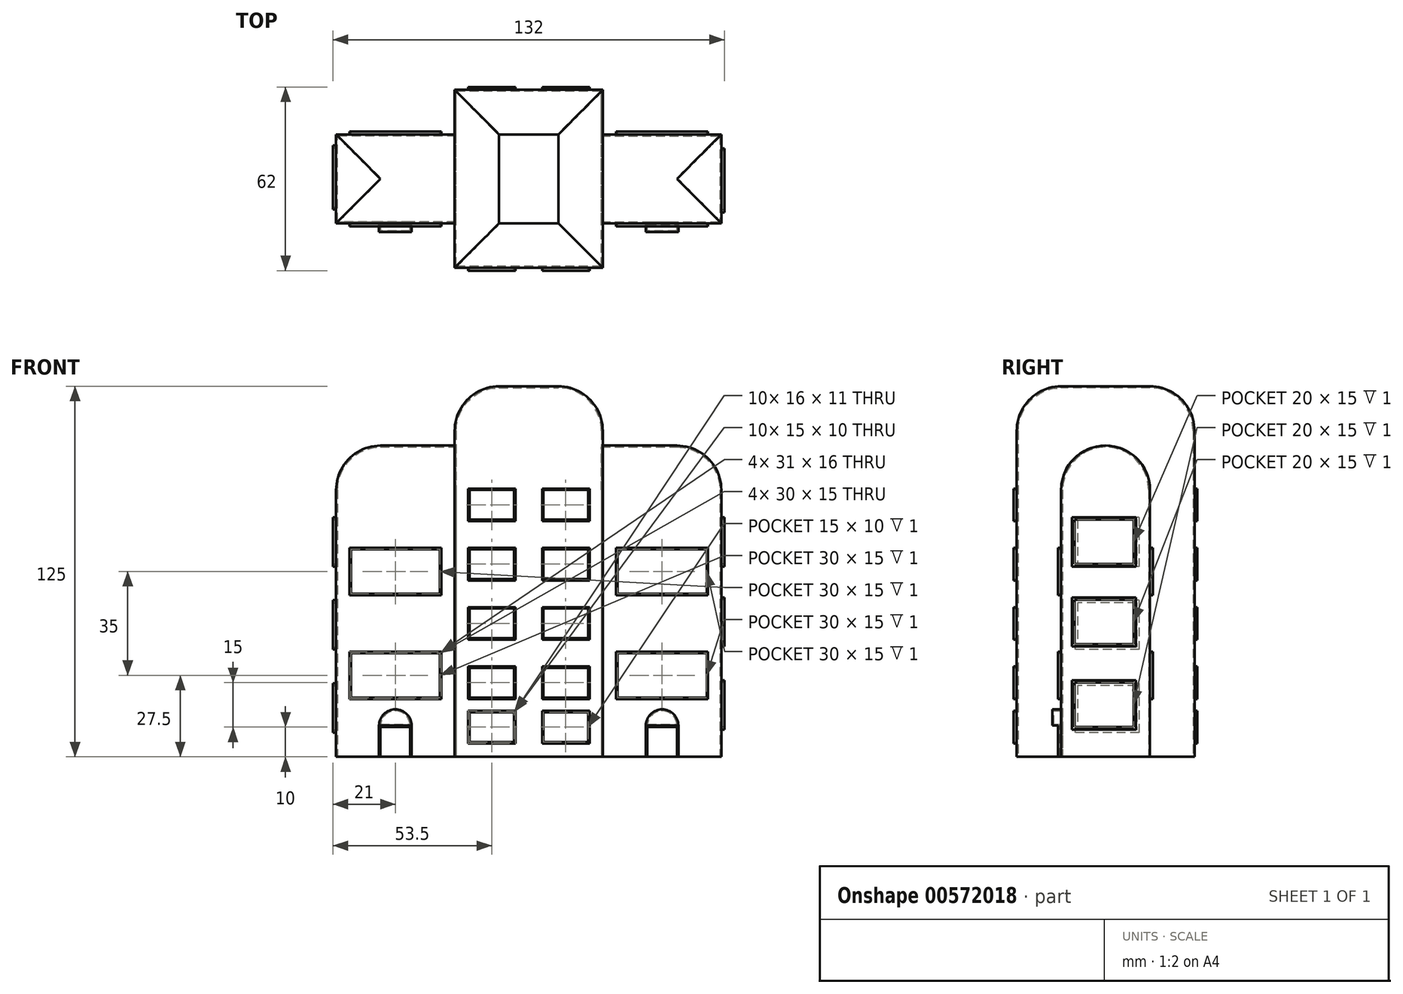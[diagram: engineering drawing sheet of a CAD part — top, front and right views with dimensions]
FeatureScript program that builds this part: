
annotation { "Feature Type Name" : "Feature", "Feature Type Description" : "" }
export const myFeature = defineFeature(function(context is Context, id is Id, definition is map)
    precondition{}
    {
        {
            var Q0;
            Q0=qCreatedBy(makeId("Top.planeOp"),FACE);
            var sketch = newSketch(context, id + "F0", { "sketchPlane" : qUnion([Q0])});
            skLineSegment(sketch, "E0.bottom", {"start": v(25, -30) * mm, "end": v(-25, -30) * mm});
            skLineSegment(sketch, "E0.top", {"start": v(25, 30) * mm, "end": v(-25, 30) * mm});
            skLineSegment(sketch, "E0.left", {"start": v(25, -30) * mm, "end": v(25, 30) * mm});
            skLineSegment(sketch, "E0.right", {"start": v(-25, -30) * mm, "end": v(-25, 30) * mm});
            skPoint(sketch, "E0.middle", {"position": v(0, 0) * mm});
            skLineSegment(sketch, "E1", {"start": v(0, 0) * mm, "end": v(90, 0) * mm, "construction": true});
            skPoint(sketch, "E1.endSnap0", {"position": v(25, 0) * mm});
            skLineSegment(sketch, "E2", {"start": v(0, 0) * mm, "end": v(-90, 0) * mm, "construction": true});
            skLineSegment(sketch, "E3.bottom", {"start": v(25, 15) * mm, "end": v(65, 15) * mm});
            skLineSegment(sketch, "E3.top", {"start": v(25, -15) * mm, "end": v(65, -15) * mm});
            skLineSegment(sketch, "E3.left", {"start": v(25, 15) * mm, "end": v(25, -15) * mm});
            skLineSegment(sketch, "E3.right", {"start": v(65, 15) * mm, "end": v(65, -15) * mm});
            skPoint(sketch, "E3.middle", {"position": v(45, 0) * mm});
            skLineSegment(sketch, "E4.bottom", {"start": v(-25, -15) * mm, "end": v(-65, -15) * mm});
            skLineSegment(sketch, "E4.top", {"start": v(-25, 15) * mm, "end": v(-65, 15) * mm});
            skLineSegment(sketch, "E4.left", {"start": v(-25, -15) * mm, "end": v(-25, 15) * mm});
            skLineSegment(sketch, "E4.right", {"start": v(-65, -15) * mm, "end": v(-65, 15) * mm});
            skPoint(sketch, "E4.middle", {"position": v(-45, 0) * mm});
            skSolve(sketch);
        }
        {
            var Q0;
            {var subQ3=sQuery(id+"F0.wireOp",EDGE,"E0.bottom");Q0=makeQuery(id+"F0.imprint","IMPRINT",FACE,{"disambiguationData":[TD([[makeQuery(id+"F0.imprint","IMPRINT",EDGE,{"derivedFrom":subQ3}),-1.0]])]});}
            extrude(context, id + "F1", {"entities" : qUnion([Q0]), "depth" : 100 * mm, "offsetDistance" : 25 * mm});
        }
        {
            var Q0;
            Q0=makeQuery(id+"F0.imprint","IMPRINT",FACE,{"disambiguationData":[TD([[makeQuery(id+"F0.imprint","IMPRINT",EDGE,{"derivedFrom":sQuery(id+"F0.wireOp",EDGE,"E4.bottom")}),-1.0]])]});
            var Q1;
            Q1=makeQuery(id+"F0.imprint","IMPRINT",FACE,{"disambiguationData":[TD([[makeQuery(id+"F0.imprint","IMPRINT",EDGE,{"derivedFrom":sQuery(id+"F0.wireOp",EDGE,"E3.bottom")}),-1.0]])]});
            extrude(context, id + "F2", {"entities" : qUnion([Q0, Q1]), "operationType" : NewBodyOperationType.ADD, "depth" : 80 * mm, "offsetDistance" : 25 * mm});
        }
        {
            var Q0;
            Q0=makeQuery(id+"F1.opExtrude","SWEPT_FACE",FACE,{"disambiguationData":[OSD([sQuery(id+"F0.wireOp",EDGE,"E0.bottom")])]});
            var sketch = newSketch(context, id + "F3", { "sketchPlane" : qUnion([Q0])});
            skLineSegment(sketch, "E5.bottom", {"start": v(-20, 90) * mm, "end": v(-5, 90) * mm});
            skLineSegment(sketch, "E5.top", {"start": v(-20, 80) * mm, "end": v(-5, 80) * mm});
            skLineSegment(sketch, "E5.left", {"start": v(-20, 90) * mm, "end": v(-20, 80) * mm});
            skLineSegment(sketch, "E5.right", {"start": v(-5, 90) * mm, "end": v(-5, 80) * mm});
            skLineSegment(sketch, "E6.bottom", {"start": v(5, 90) * mm, "end": v(20, 90) * mm});
            skLineSegment(sketch, "E6.top", {"start": v(5, 80) * mm, "end": v(20, 80) * mm});
            skLineSegment(sketch, "E6.left", {"start": v(5, 90) * mm, "end": v(5, 80) * mm});
            skLineSegment(sketch, "E6.right", {"start": v(20, 90) * mm, "end": v(20, 80) * mm});
            skLineSegment(sketch, "E7.0", {"start": v(-20.5, 90.5) * mm, "end": v(-4.5, 90.5) * mm});
            skLineSegment(sketch, "E7.1", {"start": v(-20.5, 90.5) * mm, "end": v(-20.5, 79.5) * mm});
            skLineSegment(sketch, "E7.2", {"start": v(-20.5, 79.5) * mm, "end": v(-4.5, 79.5) * mm});
            skLineSegment(sketch, "E7.3", {"start": v(-4.5, 90.5) * mm, "end": v(-4.5, 79.5) * mm});
            skLineSegment(sketch, "E8.0", {"start": v(4.5, 90.5) * mm, "end": v(20.5, 90.5) * mm});
            skLineSegment(sketch, "E8.1", {"start": v(4.5, 90.5) * mm, "end": v(4.5, 79.5) * mm});
            skLineSegment(sketch, "E8.2", {"start": v(4.5, 79.5) * mm, "end": v(20.5, 79.5) * mm});
            skLineSegment(sketch, "E8.3", {"start": v(20.5, 90.5) * mm, "end": v(20.5, 79.5) * mm});
            skLineSegment(sketch, "E9.bottom", {"start": v(-20, 70) * mm, "end": v(-5, 70) * mm});
            skLineSegment(sketch, "E9.top", {"start": v(-20, 60) * mm, "end": v(-5, 60) * mm});
            skLineSegment(sketch, "E9.left", {"start": v(-20, 70) * mm, "end": v(-20, 60) * mm});
            skLineSegment(sketch, "E9.right", {"start": v(-5, 70) * mm, "end": v(-5, 60) * mm});
            skLineSegment(sketch, "E10.bottom", {"start": v(5, 70) * mm, "end": v(20, 70) * mm});
            skLineSegment(sketch, "E10.top", {"start": v(5, 60) * mm, "end": v(20, 60) * mm});
            skLineSegment(sketch, "E10.left", {"start": v(5, 70) * mm, "end": v(5, 60) * mm});
            skLineSegment(sketch, "E10.right", {"start": v(20, 70) * mm, "end": v(20, 60) * mm});
            skLineSegment(sketch, "E11.0", {"start": v(-20.5, 70.5) * mm, "end": v(-4.5, 70.5) * mm});
            skLineSegment(sketch, "E11.1", {"start": v(-20.5, 70.5) * mm, "end": v(-20.5, 59.5) * mm});
            skLineSegment(sketch, "E11.2", {"start": v(-20.5, 59.5) * mm, "end": v(-4.5, 59.5) * mm});
            skLineSegment(sketch, "E11.3", {"start": v(-4.5, 70.5) * mm, "end": v(-4.5, 59.5) * mm});
            skLineSegment(sketch, "E12.0", {"start": v(4.5, 70.5) * mm, "end": v(4.5, 59.5) * mm});
            skLineSegment(sketch, "E12.1", {"start": v(4.5, 70.5) * mm, "end": v(20.5, 70.5) * mm});
            skLineSegment(sketch, "E12.2", {"start": v(20.5, 70.5) * mm, "end": v(20.5, 59.5) * mm});
            skLineSegment(sketch, "E12.3", {"start": v(4.5, 59.5) * mm, "end": v(20.5, 59.5) * mm});
            skLineSegment(sketch, "E13.bottom", {"start": v(-20, 50) * mm, "end": v(-5, 50) * mm});
            skLineSegment(sketch, "E13.top", {"start": v(-20, 40) * mm, "end": v(-5, 40) * mm});
            skLineSegment(sketch, "E13.left", {"start": v(-20, 50) * mm, "end": v(-20, 40) * mm});
            skLineSegment(sketch, "E13.right", {"start": v(-5, 50) * mm, "end": v(-5, 40) * mm});
            skLineSegment(sketch, "E14.bottom", {"start": v(5, 50) * mm, "end": v(20, 50) * mm});
            skLineSegment(sketch, "E14.top", {"start": v(5, 40) * mm, "end": v(20, 40) * mm});
            skLineSegment(sketch, "E14.left", {"start": v(5, 50) * mm, "end": v(5, 40) * mm});
            skLineSegment(sketch, "E14.right", {"start": v(20, 50) * mm, "end": v(20, 40) * mm});
            skLineSegment(sketch, "E15.bottom", {"start": v(-20, 30) * mm, "end": v(-5, 30) * mm});
            skLineSegment(sketch, "E15.top", {"start": v(-20, 20) * mm, "end": v(-5, 20) * mm});
            skLineSegment(sketch, "E15.left", {"start": v(-20, 30) * mm, "end": v(-20, 20) * mm});
            skLineSegment(sketch, "E15.right", {"start": v(-5, 30) * mm, "end": v(-5, 20) * mm});
            skLineSegment(sketch, "E16.bottom", {"start": v(5, 30) * mm, "end": v(20, 30) * mm});
            skLineSegment(sketch, "E16.top", {"start": v(5, 20) * mm, "end": v(20, 20) * mm});
            skLineSegment(sketch, "E16.left", {"start": v(5, 30) * mm, "end": v(5, 20) * mm});
            skLineSegment(sketch, "E16.right", {"start": v(20, 30) * mm, "end": v(20, 20) * mm});
            skLineSegment(sketch, "E17.bottom", {"start": v(-20, 15) * mm, "end": v(-5, 15) * mm});
            skLineSegment(sketch, "E17.top", {"start": v(-20, 5) * mm, "end": v(-5, 5) * mm});
            skLineSegment(sketch, "E17.left", {"start": v(-20, 15) * mm, "end": v(-20, 5) * mm});
            skLineSegment(sketch, "E17.right", {"start": v(-5, 15) * mm, "end": v(-5, 5) * mm});
            skLineSegment(sketch, "E18.bottom", {"start": v(5, 15) * mm, "end": v(20, 15) * mm});
            skLineSegment(sketch, "E18.top", {"start": v(5, 5) * mm, "end": v(20, 5) * mm});
            skLineSegment(sketch, "E18.left", {"start": v(5, 15) * mm, "end": v(5, 5) * mm});
            skLineSegment(sketch, "E18.right", {"start": v(20, 15) * mm, "end": v(20, 5) * mm});
            skLineSegment(sketch, "E19.0", {"start": v(-20.5, 50.5) * mm, "end": v(-4.5, 50.5) * mm});
            skLineSegment(sketch, "E19.1", {"start": v(-20.5, 50.5) * mm, "end": v(-20.5, 39.5) * mm});
            skLineSegment(sketch, "E19.2", {"start": v(-20.5, 39.5) * mm, "end": v(-4.5, 39.5) * mm});
            skLineSegment(sketch, "E19.3", {"start": v(-4.5, 50.5) * mm, "end": v(-4.5, 39.5) * mm});
            skLineSegment(sketch, "E20.0", {"start": v(4.5, 50.5) * mm, "end": v(4.5, 39.5) * mm});
            skLineSegment(sketch, "E20.1", {"start": v(4.5, 50.5) * mm, "end": v(20.5, 50.5) * mm});
            skLineSegment(sketch, "E20.2", {"start": v(20.5, 50.5) * mm, "end": v(20.5, 39.5) * mm});
            skLineSegment(sketch, "E20.3", {"start": v(4.5, 39.5) * mm, "end": v(20.5, 39.5) * mm});
            skLineSegment(sketch, "E21.0", {"start": v(-20.5, 30.5) * mm, "end": v(-4.5, 30.5) * mm});
            skLineSegment(sketch, "E21.1", {"start": v(-20.5, 30.5) * mm, "end": v(-20.5, 19.5) * mm});
            skLineSegment(sketch, "E21.2", {"start": v(-20.5, 19.5) * mm, "end": v(-4.5, 19.5) * mm});
            skLineSegment(sketch, "E21.3", {"start": v(-4.5, 30.5) * mm, "end": v(-4.5, 19.5) * mm});
            skLineSegment(sketch, "E22.0", {"start": v(4.5, 30.5) * mm, "end": v(20.5, 30.5) * mm});
            skLineSegment(sketch, "E22.1", {"start": v(4.5, 30.5) * mm, "end": v(4.5, 19.5) * mm});
            skLineSegment(sketch, "E22.2", {"start": v(4.5, 19.5) * mm, "end": v(20.5, 19.5) * mm});
            skLineSegment(sketch, "E22.3", {"start": v(20.5, 30.5) * mm, "end": v(20.5, 19.5) * mm});
            skLineSegment(sketch, "E23.0", {"start": v(-20.5, 15.5) * mm, "end": v(-4.5, 15.5) * mm});
            skLineSegment(sketch, "E23.1", {"start": v(-20.5, 15.5) * mm, "end": v(-20.5, 4.5) * mm});
            skLineSegment(sketch, "E23.2", {"start": v(-20.5, 4.5) * mm, "end": v(-4.5, 4.5) * mm});
            skLineSegment(sketch, "E23.3", {"start": v(-4.5, 15.5) * mm, "end": v(-4.5, 4.5) * mm});
            skLineSegment(sketch, "E24.0", {"start": v(4.5, 15.5) * mm, "end": v(20.5, 15.5) * mm});
            skLineSegment(sketch, "E24.1", {"start": v(4.5, 15.5) * mm, "end": v(4.5, 4.5) * mm});
            skLineSegment(sketch, "E24.2", {"start": v(4.5, 4.5) * mm, "end": v(20.5, 4.5) * mm});
            skLineSegment(sketch, "E24.3", {"start": v(20.5, 15.5) * mm, "end": v(20.5, 4.5) * mm});
            skSolve(sketch);
        }
        {
            var Q0;
            Q0=makeQuery(id+"F3.imprint","IMPRINT",FACE,{"disambiguationData":[TD([[makeQuery(id+"F3.imprint","IMPRINT",EDGE,{"derivedFrom":sQuery(id+"F3.wireOp",EDGE,"E5.bottom")}),1.0]])]});
            var Q1;
            Q1=makeQuery(id+"F3.imprint","IMPRINT",FACE,{"disambiguationData":[TD([[makeQuery(id+"F3.imprint","IMPRINT",EDGE,{"derivedFrom":sQuery(id+"F3.wireOp",EDGE,"E6.bottom")}),1.0]])]});
            var Q2;
            Q2=makeQuery(id+"F3.imprint","IMPRINT",FACE,{"disambiguationData":[TD([[makeQuery(id+"F3.imprint","IMPRINT",EDGE,{"derivedFrom":sQuery(id+"F3.wireOp",EDGE,"E10.bottom")}),1.0]])]});
            var Q3;
            Q3=makeQuery(id+"F3.imprint","IMPRINT",FACE,{"disambiguationData":[TD([[makeQuery(id+"F3.imprint","IMPRINT",EDGE,{"derivedFrom":sQuery(id+"F3.wireOp",EDGE,"E9.bottom")}),1.0]])]});
            var Q4;
            Q4=makeQuery(id+"F3.imprint","IMPRINT",FACE,{"disambiguationData":[TD([[makeQuery(id+"F3.imprint","IMPRINT",EDGE,{"derivedFrom":sQuery(id+"F3.wireOp",EDGE,"E13.bottom")}),1.0]])]});
            var Q5;
            Q5=makeQuery(id+"F3.imprint","IMPRINT",FACE,{"disambiguationData":[TD([[makeQuery(id+"F3.imprint","IMPRINT",EDGE,{"derivedFrom":sQuery(id+"F3.wireOp",EDGE,"E14.bottom")}),1.0]])]});
            var Q6;
            Q6=makeQuery(id+"F3.imprint","IMPRINT",FACE,{"disambiguationData":[TD([[makeQuery(id+"F3.imprint","IMPRINT",EDGE,{"derivedFrom":sQuery(id+"F3.wireOp",EDGE,"E16.bottom")}),1.0]])]});
            var Q7;
            Q7=makeQuery(id+"F3.imprint","IMPRINT",FACE,{"disambiguationData":[TD([[makeQuery(id+"F3.imprint","IMPRINT",EDGE,{"derivedFrom":sQuery(id+"F3.wireOp",EDGE,"E15.bottom")}),1.0]])]});
            var Q8;
            Q8=makeQuery(id+"F3.imprint","IMPRINT",FACE,{"disambiguationData":[TD([[makeQuery(id+"F3.imprint","IMPRINT",EDGE,{"derivedFrom":sQuery(id+"F3.wireOp",EDGE,"E17.bottom")}),1.0]])]});
            var Q9;
            Q9=makeQuery(id+"F3.imprint","IMPRINT",FACE,{"disambiguationData":[TD([[makeQuery(id+"F3.imprint","IMPRINT",EDGE,{"derivedFrom":sQuery(id+"F3.wireOp",EDGE,"E18.bottom")}),1.0]])]});
            extrude(context, id + "F4", {"entities" : qUnion([Q0, Q1, Q2, Q3, Q4, Q5, Q6, Q7, Q8, Q9]), "operationType" : NewBodyOperationType.ADD, "depth" : 1 * mm, "offsetDistance" : 25 * mm, "hasSecondDirection" : true, "secondDirectionOppositeDirection" : true, "secondDirectionDepth" : 61 * mm});
        }
        {
            var Q0;
            Q0=makeQuery(id+"F2.opExtrude","SWEPT_FACE",FACE,{"disambiguationData":[OSD([sQuery(id+"F0.wireOp",EDGE,"E4.bottom")])]});
            var sketch = newSketch(context, id + "F5", { "sketchPlane" : qUnion([Q0])});
            skLineSegment(sketch, "E25", {"start": v(-50, 0) * mm, "end": v(-50, 10) * mm});
            skLineSegment(sketch, "E26", {"start": v(-50, 10) * mm, "end": v(-45, 10) * mm});
            skLineSegment(sketch, "E27", {"start": v(-45, 10) * mm, "end": v(-45, 0) * mm});
            skLineSegment(sketch, "E28", {"start": v(-45, 10) * mm, "end": v(-40, 10) * mm});
            skLineSegment(sketch, "E29", {"start": v(-40, 10) * mm, "end": v(-40, 0) * mm});
            skLineSegment(sketch, "E30", {"start": v(-50, 0) * mm, "end": v(-40, 0) * mm});
            skLineSegment(sketch, "E31.0", {"start": v(-45, 5) * mm, "end": v(-40, 5) * mm});
            skLineSegment(sketch, "E31.1", {"start": v(-50, 5) * mm, "end": v(-45, 5) * mm});
            skLineSegment(sketch, "E32.0", {"start": v(-39.5, 10.5) * mm, "end": v(-39.5, 0) * mm});
            skLineSegment(sketch, "E32.1", {"start": v(-45, 10.5) * mm, "end": v(-39.5, 10.5) * mm});
            skLineSegment(sketch, "E32.2", {"start": v(-50.5, 10.5) * mm, "end": v(-45, 10.5) * mm});
            skLineSegment(sketch, "E32.3", {"start": v(-50.5, 0) * mm, "end": v(-50.5, 10.5) * mm});
            skArc(sketch, "E33", {"start": v(-39.5, 10.5) * mm, "mid": v(-45, 16) * mm, "end": v(-50.5, 10.5) * mm});
            skLineSegment(sketch, "E34.bottom", {"start": v(-60, 35) * mm, "end": v(-30, 35) * mm});
            skLineSegment(sketch, "E34.top", {"start": v(-60, 20) * mm, "end": v(-30, 20) * mm});
            skLineSegment(sketch, "E34.left", {"start": v(-60, 35) * mm, "end": v(-60, 20) * mm});
            skLineSegment(sketch, "E34.right", {"start": v(-30, 35) * mm, "end": v(-30, 20) * mm});
            skLineSegment(sketch, "E35.0", {"start": v(-60.5, 35.5) * mm, "end": v(-29.5, 35.5) * mm});
            skLineSegment(sketch, "E35.1", {"start": v(-60.5, 35.5) * mm, "end": v(-60.5, 19.5) * mm});
            skLineSegment(sketch, "E35.2", {"start": v(-60.5, 19.5) * mm, "end": v(-29.5, 19.5) * mm});
            skLineSegment(sketch, "E35.3", {"start": v(-29.5, 35.5) * mm, "end": v(-29.5, 19.5) * mm});
            skLineSegment(sketch, "E36.bottom", {"start": v(-60, 70) * mm, "end": v(-30, 70) * mm});
            skLineSegment(sketch, "E36.top", {"start": v(-60, 55) * mm, "end": v(-30, 55) * mm});
            skLineSegment(sketch, "E36.left", {"start": v(-60, 70) * mm, "end": v(-60, 55) * mm});
            skLineSegment(sketch, "E36.right", {"start": v(-30, 70) * mm, "end": v(-30, 55) * mm});
            skLineSegment(sketch, "E37.0", {"start": v(-60.5, 70.5) * mm, "end": v(-29.5, 70.5) * mm});
            skLineSegment(sketch, "E37.1", {"start": v(-60.5, 70.5) * mm, "end": v(-60.5, 54.5) * mm});
            skLineSegment(sketch, "E37.2", {"start": v(-60.5, 54.5) * mm, "end": v(-29.5, 54.5) * mm});
            skLineSegment(sketch, "E37.3", {"start": v(-29.5, 70.5) * mm, "end": v(-29.5, 54.5) * mm});
            skSolve(sketch);
        }
        {
            var Q0;
            {var subQ11=sQuery(id+"F5.wireOp",EDGE,"E26");Q0=makeQuery(id+"F5.imprint","IMPRINT",FACE,{"disambiguationData":[TD([[makeQuery(id+"F5.imprint","IMPRINT",EDGE,{"derivedFrom":subQ11}),1.0]])]});}
            extrude(context, id + "F6", {"entities" : qUnion([Q0]), "operationType" : NewBodyOperationType.ADD, "depth" : 1 * mm, "offsetDistance" : 25 * mm});
        }
        {
            var Q0;
            Q0=makeQuery(id+"F5.imprint","IMPRINT",FACE,{"disambiguationData":[TD([[makeQuery(id+"F5.imprint","IMPRINT",EDGE,{"derivedFrom":sQuery(id+"F5.wireOp",EDGE,"E32.1")}),1.0]])]});
            extrude(context, id + "F7", {"entities" : qUnion([Q0]), "operationType" : NewBodyOperationType.ADD, "depth" : 3 * mm, "offsetDistance" : 25 * mm});
        }
        {
            var Q0;
            {var subQ0=sQuery(id+"F5.wireOp",EDGE,"E26");Q0=makeQuery(id+"F5.imprint","IMPRINT",FACE,{"disambiguationData":[TD([[makeQuery(id+"F5.imprint","IMPRINT",EDGE,{"derivedFrom":subQ0}),-1.0]])]});}
            var Q1;
            {var subQ3=sQuery(id+"F5.wireOp",EDGE,"E31.1");Q1=makeQuery(id+"F5.imprint","IMPRINT",FACE,{"disambiguationData":[TD([[makeQuery(id+"F5.imprint","IMPRINT",EDGE,{"derivedFrom":subQ3}),-1.0]])]});}
            var Q2;
            {var subQ3=sQuery(id+"F5.wireOp",EDGE,"E31.0");Q2=makeQuery(id+"F5.imprint","IMPRINT",FACE,{"disambiguationData":[TD([[makeQuery(id+"F5.imprint","IMPRINT",EDGE,{"derivedFrom":subQ3}),-1.0]])]});}
            var Q3;
            {var subQ0=sQuery(id+"F5.wireOp",EDGE,"E28");Q3=makeQuery(id+"F5.imprint","IMPRINT",FACE,{"disambiguationData":[TD([[makeQuery(id+"F5.imprint","IMPRINT",EDGE,{"derivedFrom":subQ0}),-1.0]])]});}
            extrude(context, id + "F8", {"entities" : qUnion([Q0, Q1, Q2, Q3]), "operationType" : NewBodyOperationType.ADD, "depth" : .5 * mm, "offsetDistance" : 25 * mm});
        }
        {
            var Q0;
            Q0=makeQuery(id+"F5.imprint","IMPRINT",FACE,{"disambiguationData":[TD([[makeQuery(id+"F5.imprint","IMPRINT",EDGE,{"derivedFrom":sQuery(id+"F5.wireOp",EDGE,"E36.bottom")}),1.0]])]});
            var Q1;
            Q1=makeQuery(id+"F5.imprint","IMPRINT",FACE,{"disambiguationData":[TD([[makeQuery(id+"F5.imprint","IMPRINT",EDGE,{"derivedFrom":sQuery(id+"F5.wireOp",EDGE,"E34.bottom")}),1.0]])]});
            extrude(context, id + "F9", {"entities" : qUnion([Q0, Q1]), "operationType" : NewBodyOperationType.ADD, "depth" : 1 * mm, "offsetDistance" : 25 * mm, "hasSecondDirection" : true, "secondDirectionOppositeDirection" : true, "secondDirectionDepth" : 31 * mm});
        }
        {
            var Q0;
            Q0=makeQuery(id+"F2.opExtrude","SWEPT_FACE",FACE,{"disambiguationData":[OSD([sQuery(id+"F0.wireOp",EDGE,"E3.top")])]});
            var sketch = newSketch(context, id + "F10", { "sketchPlane" : qUnion([Q0])});
            skLineSegment(sketch, "E38.bottom", {"start": v(40, 10) * mm, "end": v(50, 10) * mm});
            skLineSegment(sketch, "E38.top", {"start": v(40, 0) * mm, "end": v(50, 0) * mm});
            skLineSegment(sketch, "E38.left", {"start": v(40, 10) * mm, "end": v(40, 0) * mm});
            skLineSegment(sketch, "E38.right", {"start": v(50, 10) * mm, "end": v(50, 0) * mm});
            skLineSegment(sketch, "E39.0", {"start": v(50.5, 10.5) * mm, "end": v(50.5, 0) * mm});
            skLineSegment(sketch, "E39.1", {"start": v(39.5, 10.5) * mm, "end": v(50.5, 10.5) * mm});
            skLineSegment(sketch, "E39.2", {"start": v(39.5, 10.5) * mm, "end": v(39.5, 0) * mm});
            skArc(sketch, "E40", {"start": v(50.5, 10.5) * mm, "mid": v(45, 16) * mm, "end": v(39.5, 10.5) * mm});
            skLineSegment(sketch, "E41.bottom", {"start": v(30, 35) * mm, "end": v(60, 35) * mm});
            skLineSegment(sketch, "E41.top", {"start": v(30, 20) * mm, "end": v(60, 20) * mm});
            skLineSegment(sketch, "E41.left", {"start": v(30, 35) * mm, "end": v(30, 20) * mm});
            skLineSegment(sketch, "E41.right", {"start": v(60, 35) * mm, "end": v(60, 20) * mm});
            skLineSegment(sketch, "E42.bottom", {"start": v(30, 70) * mm, "end": v(60, 70) * mm});
            skLineSegment(sketch, "E42.top", {"start": v(30, 55) * mm, "end": v(60, 55) * mm});
            skLineSegment(sketch, "E42.left", {"start": v(30, 70) * mm, "end": v(30, 55) * mm});
            skLineSegment(sketch, "E42.right", {"start": v(60, 70) * mm, "end": v(60, 55) * mm});
            skLineSegment(sketch, "E43.0", {"start": v(29.5, 70.5) * mm, "end": v(60.5, 70.5) * mm});
            skLineSegment(sketch, "E43.1", {"start": v(29.5, 70.5) * mm, "end": v(29.5, 54.5) * mm});
            skLineSegment(sketch, "E43.2", {"start": v(29.5, 54.5) * mm, "end": v(60.5, 54.5) * mm});
            skLineSegment(sketch, "E43.3", {"start": v(60.5, 70.5) * mm, "end": v(60.5, 54.5) * mm});
            skLineSegment(sketch, "E44.0", {"start": v(29.5, 35.5) * mm, "end": v(60.5, 35.5) * mm});
            skLineSegment(sketch, "E44.1", {"start": v(29.5, 35.5) * mm, "end": v(29.5, 19.5) * mm});
            skLineSegment(sketch, "E44.2", {"start": v(29.5, 19.5) * mm, "end": v(60.5, 19.5) * mm});
            skLineSegment(sketch, "E44.3", {"start": v(60.5, 35.5) * mm, "end": v(60.5, 19.5) * mm});
            skSolve(sketch);
        }
        {
            var Q0;
            Q0=makeQuery(id+"F10.imprint","IMPRINT",FACE,{"disambiguationData":[TD([[makeQuery(id+"F10.imprint","IMPRINT",EDGE,{"derivedFrom":sQuery(id+"F10.wireOp",EDGE,"E39.1")}),1.0]])]});
            extrude(context, id + "F11", {"entities" : qUnion([Q0]), "operationType" : NewBodyOperationType.ADD, "depth" : 3 * mm, "offsetDistance" : 25 * mm});
        }
        {
            var Q0;
            Q0=makeQuery(id+"F10.imprint","IMPRINT",FACE,{"disambiguationData":[TD([[makeQuery(id+"F10.imprint","IMPRINT",EDGE,{"derivedFrom":sQuery(id+"F10.wireOp",EDGE,"E41.bottom")}),1.0]])]});
            var Q1;
            Q1=makeQuery(id+"F10.imprint","IMPRINT",FACE,{"disambiguationData":[TD([[makeQuery(id+"F10.imprint","IMPRINT",EDGE,{"derivedFrom":sQuery(id+"F10.wireOp",EDGE,"E42.bottom")}),1.0]])]});
            extrude(context, id + "F12", {"entities" : qUnion([Q0, Q1]), "operationType" : NewBodyOperationType.ADD, "depth" : 1 * mm, "offsetDistance" : 25 * mm, "hasSecondDirection" : true, "secondDirectionOppositeDirection" : true, "secondDirectionDepth" : 31 * mm});
        }
        {
            var Q0;
            Q0=makeQuery(id+"F10.imprint","IMPRINT",FACE,{"disambiguationData":[TD([[makeQuery(id+"F10.imprint","IMPRINT",EDGE,{"derivedFrom":sQuery(id+"F10.wireOp",EDGE,"E38.bottom")}),1.0]])]});
            extrude(context, id + "F13", {"entities" : qUnion([Q0]), "operationType" : NewBodyOperationType.ADD, "depth" : 1 * mm, "offsetDistance" : 25 * mm});
        }
        {
            var Q0;
            Q0=makeQuery(id+"F2.opExtrude","CAP_FACE",FACE,{"disambiguationData":[OSD([sQuery(id+"F0.wireOp",EDGE,"E3.bottom"),sQuery(id+"F0.wireOp",EDGE,"E3.top"),sQuery(id+"F0.wireOp",EDGE,"E3.left"),sQuery(id+"F0.wireOp",EDGE,"E3.right")])],"isStart":false});
            var sketch = newSketch(context, id + "F14", { "sketchPlane" : qUnion([Q0])});
            skLineSegment(sketch, "E45.bottom", {"start": v(65, -15) * mm, "end": v(25, -15) * mm});
            skLineSegment(sketch, "E45.top", {"start": v(65, 15) * mm, "end": v(25, 15) * mm});
            skLineSegment(sketch, "E45.left", {"start": v(65, -15) * mm, "end": v(65, 15) * mm});
            skLineSegment(sketch, "E45.right", {"start": v(25, -15) * mm, "end": v(25, 15) * mm});
            skSolve(sketch);
        }
        {
            var Q0;
            Q0=makeQuery(id+"F14.imprint","IMPRINT",FACE,{"disambiguationData":[TD([[makeQuery(id+"F14.imprint","IMPRINT",EDGE,{"derivedFrom":sQuery(id+"F14.wireOp",EDGE,"E45.bottom")}),1.0]])]});
            extrude(context, id + "F15", {"entities" : qUnion([Q0]), "operationType" : NewBodyOperationType.ADD, "depth" : 25 * mm, "offsetDistance" : 25 * mm});
        }
        {
            var Q0;
            Q0=makeQuery(id+"F15.opExtrude","CAP_EDGE",EDGE,{"disambiguationData":[OSD([sQuery(id+"F14.wireOp",EDGE,"E45.top")])],"isStart":false});
            var Q1;
            Q1=makeQuery(id+"F15.opExtrude","CAP_EDGE",EDGE,{"disambiguationData":[OSD([sQuery(id+"F14.wireOp",EDGE,"E45.left")])],"isStart":false});
            var Q2;
            Q2=makeQuery(id+"F15.opExtrude","CAP_EDGE",EDGE,{"disambiguationData":[OSD([sQuery(id+"F14.wireOp",EDGE,"E45.bottom")])],"isStart":false});
            fillet(context, id + "F16", {"entities" : qUnion([Q0, Q1, Q2]), "radius" : 15 * mm, "tangentPropagation" : true, "allowEdgeOverflow" : false});
        }
        {
            var Q0;
            Q0=makeQuery(id+"F2.opExtrude","CAP_FACE",FACE,{"disambiguationData":[OSD([sQuery(id+"F0.wireOp",EDGE,"E4.bottom"),sQuery(id+"F0.wireOp",EDGE,"E4.top"),sQuery(id+"F0.wireOp",EDGE,"E4.left"),sQuery(id+"F0.wireOp",EDGE,"E4.right")])],"isStart":false});
            var sketch = newSketch(context, id + "F17", { "sketchPlane" : qUnion([Q0])});
            skLineSegment(sketch, "E46.bottom", {"start": v(-65, 15) * mm, "end": v(-25, 15) * mm});
            skLineSegment(sketch, "E46.top", {"start": v(-65, -15) * mm, "end": v(-25, -15) * mm});
            skLineSegment(sketch, "E46.left", {"start": v(-65, 15) * mm, "end": v(-65, -15) * mm});
            skLineSegment(sketch, "E46.right", {"start": v(-25, 15) * mm, "end": v(-25, -15) * mm});
            skSolve(sketch);
        }
        {
            var Q0;
            Q0 = qSketchRegion(id + "F17", true);
            extrude(context, id + "F18", {"entities" : qUnion([Q0]), "operationType" : NewBodyOperationType.ADD, "depth" : 25 * mm, "offsetDistance" : 25 * mm});
        }
        {
            var Q0;
            Q0=makeQuery(id+"F18.opExtrude","CAP_EDGE",EDGE,{"disambiguationData":[OSD([sQuery(id+"F17.wireOp",EDGE,"E46.left")])],"isStart":false});
            var Q1;
            Q1=makeQuery(id+"F18.opExtrude","CAP_EDGE",EDGE,{"disambiguationData":[OSD([sQuery(id+"F17.wireOp",EDGE,"E46.bottom")])],"isStart":false});
            var Q2;
            Q2=makeQuery(id+"F18.opExtrude","CAP_EDGE",EDGE,{"disambiguationData":[OSD([sQuery(id+"F17.wireOp",EDGE,"E46.top")])],"isStart":false});
            fillet(context, id + "F19", {"entities" : qUnion([Q0, Q1, Q2]), "radius" : 15 * mm, "tangentPropagation" : true, "allowEdgeOverflow" : false});
        }
        {
            var Q0;
            Q0=makeQuery(id+"F1.opExtrude","CAP_FACE",FACE,{"disambiguationData":[OSD([sQuery(id+"F0.wireOp",EDGE,"E0.bottom"),sQuery(id+"F0.wireOp",EDGE,"E0.top"),sQuery(id+"F0.wireOp",EDGE,"E0.left"),sQuery(id+"F0.wireOp",EDGE,"E0.right"),sQuery(id+"F0.wireOp",EDGE,"E3.left"),sQuery(id+"F0.wireOp",EDGE,"E4.left")])],"isStart":false});
            var sketch = newSketch(context, id + "F20", { "sketchPlane" : qUnion([Q0])});
            skLineSegment(sketch, "E47.bottom", {"start": v(-25, 30) * mm, "end": v(25, 30) * mm});
            skLineSegment(sketch, "E47.top", {"start": v(-25, -30) * mm, "end": v(25, -30) * mm});
            skLineSegment(sketch, "E47.left", {"start": v(-25, 30) * mm, "end": v(-25, -30) * mm});
            skLineSegment(sketch, "E47.right", {"start": v(25, 30) * mm, "end": v(25, -30) * mm});
            skSolve(sketch);
        }
        {
            var Q0;
            {var subQ4=sQuery(id+"F20.wireOp",EDGE,"E47.bottom");Q0=makeQuery(id+"F20.imprint","IMPRINT",FACE,{"disambiguationData":[TD([[makeQuery(id+"F20.imprint","IMPRINT",EDGE,{"derivedFrom":subQ4}),1.0]])]});}
            extrude(context, id + "F21", {"entities" : qUnion([Q0]), "operationType" : NewBodyOperationType.ADD, "depth" : 25 * mm, "offsetDistance" : 25 * mm});
        }
        {
            var Q0;
            Q0=makeQuery(id+"F21.opExtrude","CAP_EDGE",EDGE,{"disambiguationData":[OSD([sQuery(id+"F20.wireOp",EDGE,"E47.left")])],"isStart":false});
            var Q1;
            Q1=makeQuery(id+"F21.opExtrude","CAP_EDGE",EDGE,{"disambiguationData":[OSD([sQuery(id+"F20.wireOp",EDGE,"E47.bottom")])],"isStart":false});
            var Q2;
            Q2=makeQuery(id+"F21.opExtrude","CAP_EDGE",EDGE,{"disambiguationData":[OSD([sQuery(id+"F20.wireOp",EDGE,"E47.right")])],"isStart":false});
            var Q3;
            Q3=makeQuery(id+"F21.opExtrude","CAP_EDGE",EDGE,{"disambiguationData":[OSD([sQuery(id+"F20.wireOp",EDGE,"E47.top")])],"isStart":false});
            fillet(context, id + "F22", {"entities" : qUnion([Q0, Q1, Q2, Q3]), "radius" : 15 * mm, "tangentPropagation" : true, "allowEdgeOverflow" : false});
        }
        {
            var Q0;
            Q0=makeQuery(id+"F15.boolean.opBoolean","MERGE",FACE,{"derivedFrom":[makeQuery(id+"F2.opExtrude","SWEPT_FACE",FACE,{"disambiguationData":[OSD([sQuery(id+"F0.wireOp",EDGE,"E3.right")])]}),makeQuery(id+"F15.opExtrude","SWEPT_FACE",FACE,{"disambiguationData":[OSD([sQuery(id+"F14.wireOp",EDGE,"E45.left")])]})]});
            var sketch = newSketch(context, id + "F23", { "sketchPlane" : qUnion([Q0])});
            skLineSegment(sketch, "E48.bottom", {"start": v(-10.5, 80) * mm, "end": v(9.5, 80) * mm});
            skLineSegment(sketch, "E48.top", {"start": v(-10.5, 65) * mm, "end": v(9.5, 65) * mm});
            skLineSegment(sketch, "E48.left", {"start": v(-10.5, 80) * mm, "end": v(-10.5, 65) * mm});
            skLineSegment(sketch, "E48.right", {"start": v(9.5, 80) * mm, "end": v(9.5, 65) * mm});
            skLineSegment(sketch, "E49.0", {"start": v(-11.3, 80.8) * mm, "end": v(10.3, 80.8) * mm});
            skLineSegment(sketch, "E49.1", {"start": v(-11.3, 80.8) * mm, "end": v(-11.3, 64.2) * mm});
            skLineSegment(sketch, "E49.2", {"start": v(-11.3, 64.2) * mm, "end": v(10.3, 64.2) * mm});
            skLineSegment(sketch, "E49.3", {"start": v(10.3, 80.8) * mm, "end": v(10.3, 64.2) * mm});
            skLineSegment(sketch, "E50.bottom", {"start": v(-10.5, 25) * mm, "end": v(9.5, 25) * mm});
            skLineSegment(sketch, "E50.top", {"start": v(-10.5, 10) * mm, "end": v(9.5, 10) * mm});
            skLineSegment(sketch, "E50.left", {"start": v(-10.5, 25) * mm, "end": v(-10.5, 10) * mm});
            skLineSegment(sketch, "E50.right", {"start": v(9.5, 25) * mm, "end": v(9.5, 10) * mm});
            skLineSegment(sketch, "E51.0", {"start": v(-11.3, 25.8) * mm, "end": v(10.3, 25.8) * mm});
            skLineSegment(sketch, "E51.1", {"start": v(-11.3, 25.8) * mm, "end": v(-11.3, 9.2) * mm});
            skLineSegment(sketch, "E51.2", {"start": v(-11.3, 9.2) * mm, "end": v(10.3, 9.2) * mm});
            skLineSegment(sketch, "E51.3", {"start": v(10.3, 25.8) * mm, "end": v(10.3, 9.2) * mm});
            skLineSegment(sketch, "E52.bottom", {"start": v(-10.5, 53) * mm, "end": v(9.5, 53) * mm});
            skLineSegment(sketch, "E52.top", {"start": v(-10.5, 38) * mm, "end": v(9.5, 38) * mm});
            skLineSegment(sketch, "E52.left", {"start": v(-10.5, 53) * mm, "end": v(-10.5, 38) * mm});
            skLineSegment(sketch, "E52.right", {"start": v(9.5, 53) * mm, "end": v(9.5, 38) * mm});
            skLineSegment(sketch, "E53.0", {"start": v(-11.3, 53.8) * mm, "end": v(10.3, 53.8) * mm});
            skLineSegment(sketch, "E53.1", {"start": v(-11.3, 53.8) * mm, "end": v(-11.3, 37.2) * mm});
            skLineSegment(sketch, "E53.2", {"start": v(-11.3, 37.2) * mm, "end": v(10.3, 37.2) * mm});
            skLineSegment(sketch, "E53.3", {"start": v(10.3, 53.8) * mm, "end": v(10.3, 37.2) * mm});
            skSolve(sketch);
        }
        {
            var Q0;
            Q0=makeQuery(id+"F23.imprint","IMPRINT",FACE,{"disambiguationData":[TD([[makeQuery(id+"F23.imprint","IMPRINT",EDGE,{"derivedFrom":sQuery(id+"F23.wireOp",EDGE,"E48.bottom")}),1.0]])]});
            var Q1;
            Q1=makeQuery(id+"F23.imprint","IMPRINT",FACE,{"disambiguationData":[TD([[makeQuery(id+"F23.imprint","IMPRINT",EDGE,{"derivedFrom":sQuery(id+"F23.wireOp",EDGE,"E52.bottom")}),1.0]])]});
            var Q2;
            Q2=makeQuery(id+"F23.imprint","IMPRINT",FACE,{"disambiguationData":[TD([[makeQuery(id+"F23.imprint","IMPRINT",EDGE,{"derivedFrom":sQuery(id+"F23.wireOp",EDGE,"E50.bottom")}),1.0]])]});
            extrude(context, id + "F24", {"entities" : qUnion([Q0, Q1, Q2]), "operationType" : NewBodyOperationType.ADD, "depth" : 1 * mm, "offsetDistance" : 25 * mm});
        }
        {
            var Q0;
            Q0=makeQuery(id+"F18.boolean.opBoolean","MERGE",FACE,{"derivedFrom":[makeQuery(id+"F2.opExtrude","SWEPT_FACE",FACE,{"disambiguationData":[OSD([sQuery(id+"F0.wireOp",EDGE,"E4.right")])]}),makeQuery(id+"F18.opExtrude","SWEPT_FACE",FACE,{"disambiguationData":[OSD([sQuery(id+"F17.wireOp",EDGE,"E46.left")])]})]});
            var sketch = newSketch(context, id + "F25", { "sketchPlane" : qUnion([Q0])});
            skLineSegment(sketch, "E54.bottom", {"start": v(-10.5, 80) * mm, "end": v(9.5, 80) * mm});
            skLineSegment(sketch, "E54.top", {"start": v(-10.5, 65) * mm, "end": v(9.5, 65) * mm});
            skLineSegment(sketch, "E54.left", {"start": v(-10.5, 80) * mm, "end": v(-10.5, 65) * mm});
            skLineSegment(sketch, "E54.right", {"start": v(9.5, 80) * mm, "end": v(9.5, 65) * mm});
            skLineSegment(sketch, "E55.bottom", {"start": v(-10.5, 52) * mm, "end": v(9.5, 52) * mm});
            skLineSegment(sketch, "E55.top", {"start": v(-10.5, 37) * mm, "end": v(9.5, 37) * mm});
            skLineSegment(sketch, "E55.left", {"start": v(-10.5, 52) * mm, "end": v(-10.5, 37) * mm});
            skLineSegment(sketch, "E55.right", {"start": v(9.5, 52) * mm, "end": v(9.5, 37) * mm});
            skLineSegment(sketch, "E56.bottom", {"start": v(-10.5, 24) * mm, "end": v(9.5, 24) * mm});
            skLineSegment(sketch, "E56.top", {"start": v(-10.5, 9) * mm, "end": v(9.5, 9) * mm});
            skLineSegment(sketch, "E56.left", {"start": v(-10.5, 24) * mm, "end": v(-10.5, 9) * mm});
            skLineSegment(sketch, "E56.right", {"start": v(9.5, 24) * mm, "end": v(9.5, 9) * mm});
            skLineSegment(sketch, "E57.0", {"start": v(-11.3, 80.8) * mm, "end": v(10.3, 80.8) * mm});
            skLineSegment(sketch, "E57.1", {"start": v(-11.3, 80.8) * mm, "end": v(-11.3, 64.2) * mm});
            skLineSegment(sketch, "E57.2", {"start": v(-11.3, 64.2) * mm, "end": v(10.3, 64.2) * mm});
            skLineSegment(sketch, "E57.3", {"start": v(10.3, 80.8) * mm, "end": v(10.3, 64.2) * mm});
            skLineSegment(sketch, "E58.0", {"start": v(-11.3, 52.8) * mm, "end": v(10.3, 52.8) * mm});
            skLineSegment(sketch, "E58.1", {"start": v(-11.3, 52.8) * mm, "end": v(-11.3, 36.2) * mm});
            skLineSegment(sketch, "E58.2", {"start": v(-11.3, 36.2) * mm, "end": v(10.3, 36.2) * mm});
            skLineSegment(sketch, "E58.3", {"start": v(10.3, 52.8) * mm, "end": v(10.3, 36.2) * mm});
            skLineSegment(sketch, "E59.0", {"start": v(-15.5, 24) * mm, "end": v(-15.5, 9) * mm});
            skLineSegment(sketch, "E60.0", {"start": v(-11.3, 8.2) * mm, "end": v(10.3, 8.2) * mm});
            skLineSegment(sketch, "E60.1", {"start": v(-11.3, 24.8) * mm, "end": v(-11.3, 8.2) * mm});
            skLineSegment(sketch, "E60.2", {"start": v(-11.3, 24.8) * mm, "end": v(10.3, 24.8) * mm});
            skLineSegment(sketch, "E60.3", {"start": v(10.3, 24.8) * mm, "end": v(10.3, 8.2) * mm});
            skSolve(sketch);
        }
        {
            var Q0;
            Q0=makeQuery(id+"F25.imprint","IMPRINT",FACE,{"disambiguationData":[TD([[makeQuery(id+"F25.imprint","IMPRINT",EDGE,{"derivedFrom":sQuery(id+"F25.wireOp",EDGE,"E55.bottom")}),1.0]])]});
            var Q1;
            Q1=makeQuery(id+"F25.imprint","IMPRINT",FACE,{"disambiguationData":[TD([[makeQuery(id+"F25.imprint","IMPRINT",EDGE,{"derivedFrom":sQuery(id+"F25.wireOp",EDGE,"E56.bottom")}),1.0]])]});
            var Q2;
            Q2=makeQuery(id+"F25.imprint","IMPRINT",FACE,{"disambiguationData":[TD([[makeQuery(id+"F25.imprint","IMPRINT",EDGE,{"derivedFrom":sQuery(id+"F25.wireOp",EDGE,"E54.bottom")}),1.0]])]});
            extrude(context, id + "F26", {"entities" : qUnion([Q0, Q1, Q2]), "operationType" : NewBodyOperationType.ADD, "depth" : 1 * mm, "offsetDistance" : 25 * mm});
        }
        {
            var Q0;
            {var subQ1=sQuery(id+"F0.wireOp",EDGE,"E3.top");var subQ2=makeQuery(id+"F2.opExtrude","CAP_EDGE",EDGE,{"disambiguationData":[OSD([subQ1])],"isStart":true});var subQ3=sQuery(id+"F5.wireOp",EDGE,"E30");var subQ4=sQuery(id+"F0.wireOp",EDGE,"E4.bottom");var subQ5=makeQuery(id+"F2.opExtrude","CAP_EDGE",EDGE,{"disambiguationData":[OSD([subQ4])],"isStart":true});var subQ6=sQuery(id+"F0.wireOp",EDGE,"E4.left");var subQ7=sQuery(id+"F0.wireOp",EDGE,"E3.left");Q0=makeQuery(id+"F13.boolean.opBoolean","MERGE",FACE,{"derivedFrom":[makeQuery(id+"F8.boolean.opBoolean","MERGE",FACE,{"derivedFrom":[makeQuery(id+"F6.boolean.opBoolean","MERGE",FACE,{"derivedFrom":[makeQuery(id+"F2.boolean.opBoolean","MERGE",FACE,{"derivedFrom":[makeQuery(id+"F1.opExtrude","CAP_FACE",FACE,{"disambiguationData":[OSD([sQuery(id+"F0.wireOp",EDGE,"E0.bottom"),sQuery(id+"F0.wireOp",EDGE,"E0.top"),sQuery(id+"F0.wireOp",EDGE,"E0.left"),sQuery(id+"F0.wireOp",EDGE,"E0.right"),subQ7,subQ6])],"isStart":true}),makeQuery(id+"F2.opExtrude","CAP_FACE",FACE,{"disambiguationData":[OSD([sQuery(id+"F0.wireOp",EDGE,"E3.bottom"),subQ1,subQ7,sQuery(id+"F0.wireOp",EDGE,"E3.right")])],"isStart":true}),makeQuery(id+"F2.opExtrude","CAP_FACE",FACE,{"disambiguationData":[OSD([subQ4,sQuery(id+"F0.wireOp",EDGE,"E4.top"),subQ6,sQuery(id+"F0.wireOp",EDGE,"E4.right")])],"isStart":true})]}),makeQuery(id+"F6.opExtrude","SWEPT_FACE",FACE,{"disambiguationData":[OSD([subQ4]),TDD([makeQuery(id+"F5.imprint","IMPRINT",EDGE,{"disambiguationData":[TD([[makeQuery(id+"F5.imprint","INTERSECT",VERTEX,{"derivedFrom":[subQ5,sQuery(id+"F5.wireOp",EDGE,"E32.3")]}),1.0]])],"derivedFrom":subQ5})])]}),makeQuery(id+"F6.opExtrude","SWEPT_FACE",FACE,{"disambiguationData":[OSD([subQ4]),TDD([makeQuery(id+"F5.imprint","IMPRINT",EDGE,{"disambiguationData":[TD([[makeQuery(id+"F5.imprint","INTERSECT",VERTEX,{"derivedFrom":[subQ5,sQuery(id+"F5.wireOp",EDGE,"E32.0")]}),-1.0]])],"derivedFrom":subQ5})])]})]}),makeQuery(id+"F8.opExtrude","SWEPT_FACE",FACE,{"disambiguationData":[OSD([subQ3])]})]}),makeQuery(id+"F13.opExtrude","SWEPT_FACE",FACE,{"disambiguationData":[OSD([subQ1]),TDD([makeQuery(id+"F10.imprint","IMPRINT",EDGE,{"disambiguationData":[TD([[makeQuery(id+"F10.imprint","INTERSECT",VERTEX,{"derivedFrom":[subQ2,sQuery(id+"F10.wireOp",EDGE,"E39.2")]}),-1.0]])],"derivedFrom":subQ2})])]}),makeQuery(id+"F13.opExtrude","SWEPT_FACE",FACE,{"disambiguationData":[OSD([subQ1]),TDD([makeQuery(id+"F10.imprint","IMPRINT",EDGE,{"disambiguationData":[TD([[makeQuery(id+"F10.imprint","INTERSECT",VERTEX,{"derivedFrom":[subQ2,sQuery(id+"F10.wireOp",EDGE,"E39.0")]}),1.0]])],"derivedFrom":subQ2})])]})]});}
            var Q1;
            Q1=makeQuery(id+"F21.opExtrude","CAP_FACE",FACE,{"disambiguationData":[OSD([sQuery(id+"F20.wireOp",EDGE,"E47.bottom"),sQuery(id+"F20.wireOp",EDGE,"E47.top"),sQuery(id+"F20.wireOp",EDGE,"E47.left"),sQuery(id+"F20.wireOp",EDGE,"E47.right")])],"isStart":false});
            shell(context, id + "F27", {"entities" : qUnion([Q0, Q1]), "thickness" : .5 * mm});
        }
    });
